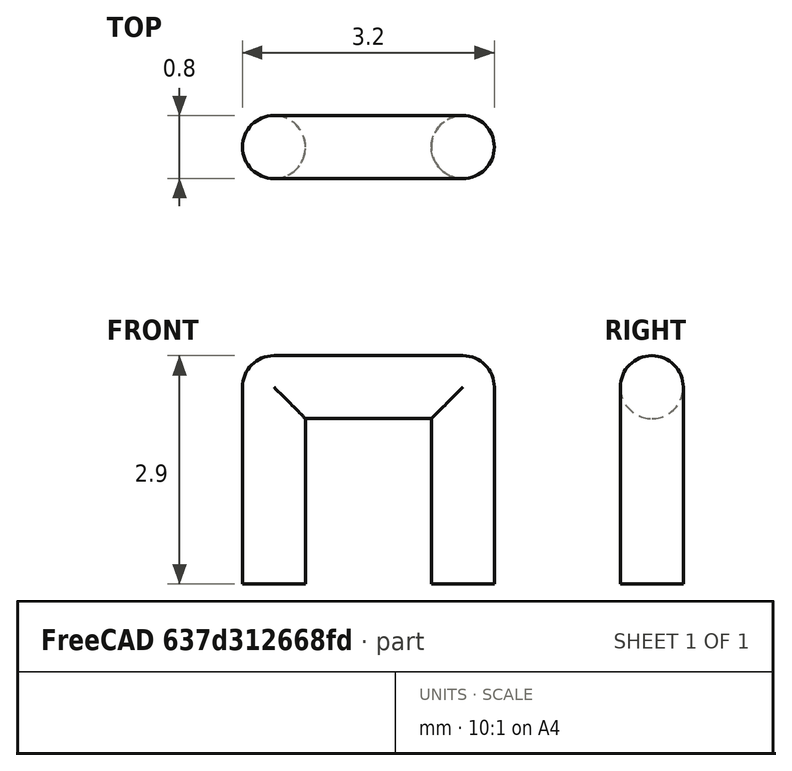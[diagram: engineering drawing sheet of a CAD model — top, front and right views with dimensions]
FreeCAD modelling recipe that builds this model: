
FCSTD DOCUMENT  (FreeCAD 0.18R)
Label: TVDT18-050CW-T
License: All rights reserved
LicenseURL: http://en.wikipedia.org/wiki/All_rights_reserved
objects: Part::Cylinder×3, Part::Sphere×2, Part::MultiFuse×1
note: 6 computed .brp shape members not serialized (recipe doc carries the construction recipe); baked Part::Feature solids carry a one-line shape summary decoded from their .brp

FEATURE [Part::Cylinder] Cylinder002  label="Jumper_2.40mm_001"
  Angle = 360
  AttacherType = Attacher::AttachEngine3D
  Height = 2.5
  Placement = pos=(0,0,-2.1) rot=(0,0,1;0rad)
  Radius = 0.4
FEATURE [Part::Cylinder] Cylinder003  label="Jumper_2.40mm_002"
  Angle = 360
  AttacherType = Attacher::AttachEngine3D
  Height = 2.4
  Placement = pos=(0,0,0.4) rot=(0,1,0;1.5708rad)
  Radius = 0.4
FEATURE [Part::Cylinder] Cylinder004  label="Jumper_2.40mm_003"
  Angle = 360
  AttacherType = Attacher::AttachEngine3D
  Height = 2.5
  Placement = pos=(2.4,0,-2.1) rot=(0,0,1;0rad)
  Radius = 0.4
FEATURE [Part::Sphere] Sphere  label="Jumper_2.40mm_004"
  Angle1 = -90
  Angle2 = 90
  Angle3 = 90
  AttacherType = Attacher::AttachEngine3D
  Placement = pos=(0,0,0.4) rot=(0,0.707107,0.707107;3.14159rad)
  Radius = 0.4
FEATURE [Part::Sphere] Sphere001  label="Jumper_2.40mm_005"
  Angle1 = -90
  Angle2 = 90
  Angle3 = 90
  AttacherType = Attacher::AttachEngine3D
  Placement = pos=(2.4,0,0.4) rot=(1,0,0;1.5708rad)
  Radius = 0.4
FEATURE [Part::MultiFuse] Fusion001  label="Jumper_2.40mm"
  Shapes = -> [Cylinder002,Cylinder003,Cylinder004,Sphere,Sphere001]
